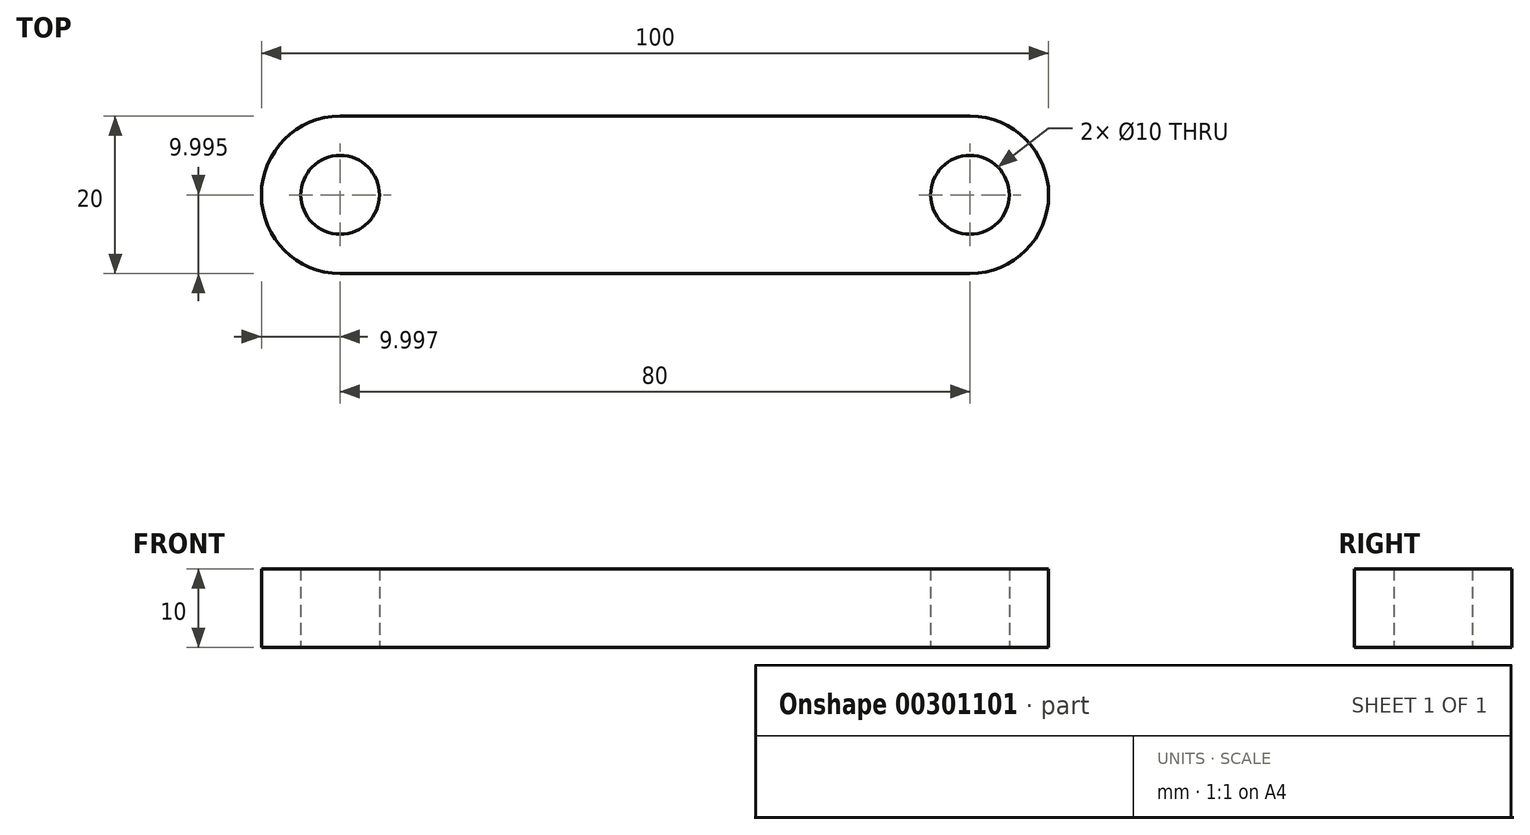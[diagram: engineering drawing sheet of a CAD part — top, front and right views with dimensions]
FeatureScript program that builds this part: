
annotation { "Feature Type Name" : "Feature", "Feature Type Description" : "" }
export const myFeature = defineFeature(function(context is Context, id is Id, definition is map)
    precondition{}
    {
        {
            var Q0;
            Q0=qCreatedBy(makeId("Top.planeOp"),FACE);
            var sketch = newSketch(context, id + "F0", { "sketchPlane" : qUnion([Q0])});
            skLineSegment(sketch, "E0", {"start": v(-27.27, 27.76) * mm, "end": v(52.73, 27.76) * mm});
            skLineSegment(sketch, "E1", {"start": v(-27.27, 7.76) * mm, "end": v(52.73, 7.76) * mm});
            skArc(sketch, "E2", {"start": v(-27.27, 27.76) * mm, "mid": v(-37.27, 17.76) * mm, "end": v(-27.27, 7.76) * mm});
            skArc(sketch, "E3", {"start": v(52.73, 27.76) * mm, "mid": v(62.73, 17.76) * mm, "end": v(52.73, 7.76) * mm});
            skCircle(sketch, "E4", {"center": v(-27.27, 17.76) * mm, "radius": 5 * mm});
            skCircle(sketch, "E5", {"center": v(52.73, 17.76) * mm, "radius": 5 * mm});
            skSolve(sketch);
        }
        {
            var Q0;
            Q0=makeQuery(id+"F0.imprint","IMPRINT",FACE,{"disambiguationData":[TD([[makeQuery(id+"F0.imprint","IMPRINT",EDGE,{"derivedFrom":sQuery(id+"F0.wireOp",EDGE,"E0")}),-1.0]])]});
            extrude(context, id + "F1", {"entities" : qUnion([Q0]), "depth" : 10 * mm});
        }
    });
